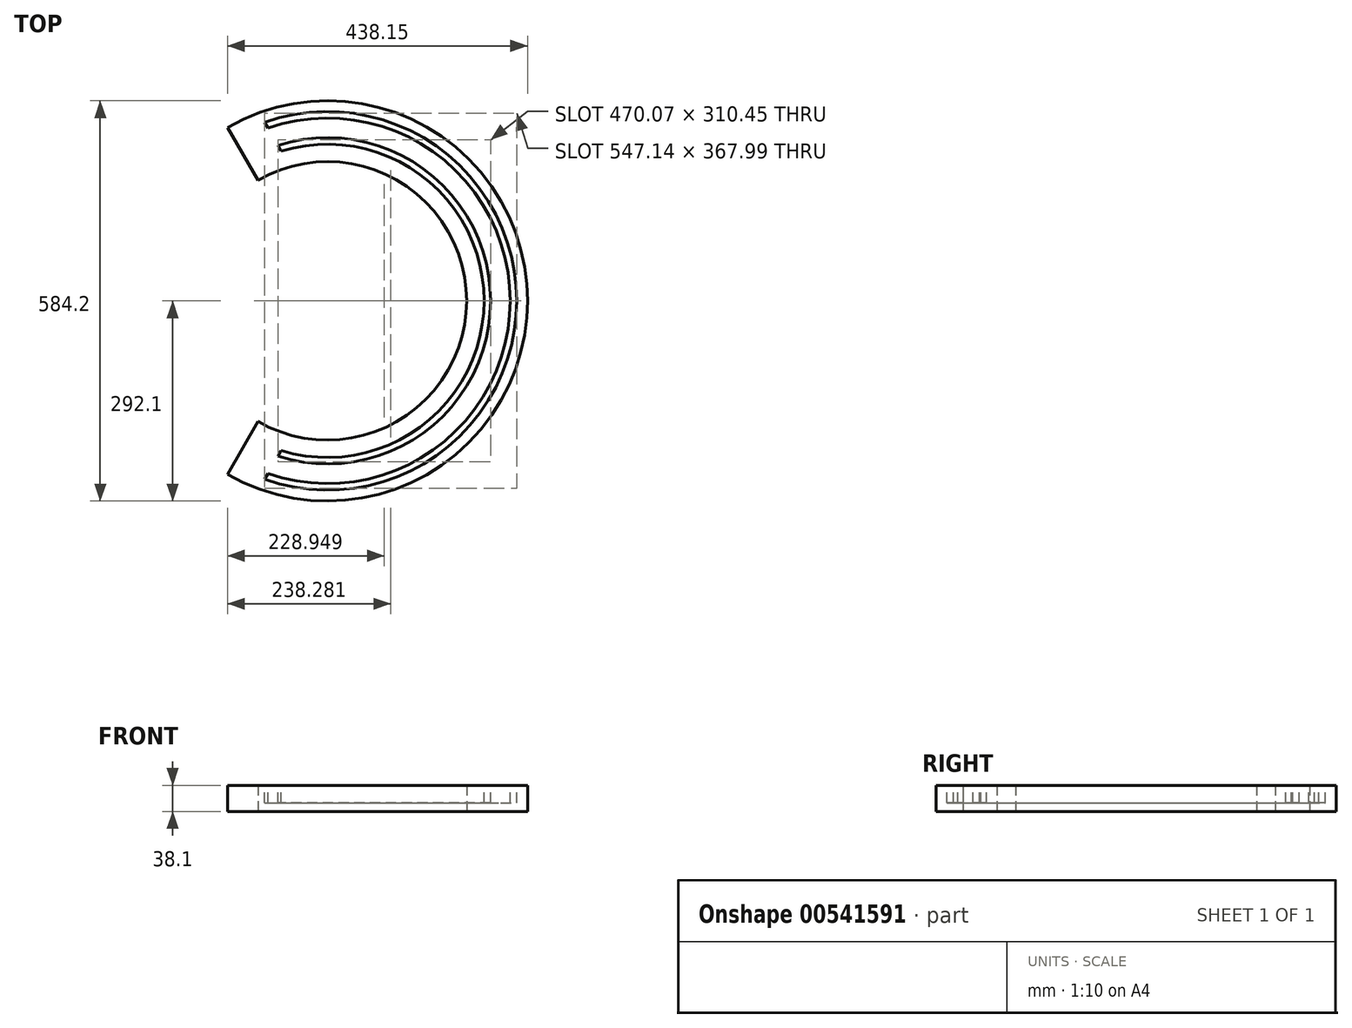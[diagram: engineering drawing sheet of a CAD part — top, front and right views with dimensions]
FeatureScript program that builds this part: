
annotation { "Feature Type Name" : "Feature", "Feature Type Description" : "" }
export const myFeature = defineFeature(function(context is Context, id is Id, definition is map)
    precondition{}
    {
        {
            var Q0;
            Q0=qCreatedBy(makeId("Top.planeOp"),FACE);
            var sketch = newSketch(context, id + "F0", { "sketchPlane" : qUnion([Q0])});
            skArc(sketch, "E0", {"start": v(-101.6, -175.98) * mm, "mid": v(203.2, 0) * mm, "end": v(-101.6, 175.98) * mm});
            skArc(sketch, "E1", {"start": v(-146.05, -252.97) * mm, "mid": v(292.1, 0) * mm, "end": v(-146.05, 252.97) * mm});
            skLineSegment(sketch, "E2", {"start": v(-101.6, -175.98) * mm, "end": v(-146.05, -252.97) * mm});
            skLineSegment(sketch, "E3", {"start": v(-101.6, 175.98) * mm, "end": v(-146.05, 252.97) * mm});
            skSolve(sketch);
        }
        {
            var Q0;
            Q0=makeQuery(id+"F0.imprint","IMPRINT",FACE,{"disambiguationData":[TD([[makeQuery(id+"F0.imprint","IMPRINT",EDGE,{"derivedFrom":sQuery(id+"F0.wireOp",EDGE,"E0")}),-1.0]])]});
            extrude(context, id + "F1", {"entities" : qUnion([Q0]), "depth" : 38.1 * mm, "offsetDistance" : 25.4 * mm});
        }
        {
            var Q0;
            Q0=makeQuery(id+"F1.opExtrude","CAP_FACE",FACE,{"disambiguationData":[OSD([sQuery(id+"F0.wireOp",EDGE,"E0"),sQuery(id+"F0.wireOp",EDGE,"E1"),sQuery(id+"F0.wireOp",EDGE,"E2"),sQuery(id+"F0.wireOp",EDGE,"E3")])],"isStart":false});
            var sketch = newSketch(context, id + "F2", { "sketchPlane" : qUnion([Q0])});
            skArc(sketch, "E4", {"start": v(-67.45, -218.42) * mm, "mid": v(228.6, 0) * mm, "end": v(-67.45, 218.42) * mm});
            skLineSegment(sketch, "E5", {"start": v(-101.6, 175.98) * mm, "end": v(-146.05, 252.97) * mm});
            skLineSegment(sketch, "E6", {"start": v(-101.6, -175.98) * mm, "end": v(-146.05, -252.97) * mm});
            skArc(sketch, "E7", {"start": v(-72.33, -226.87) * mm, "mid": v(238.13, 0) * mm, "end": v(-72.33, 226.87) * mm});
            skArc(sketch, "E8", {"start": v(-86.91, -252.14) * mm, "mid": v(266.7, 0) * mm, "end": v(-86.91, 252.14) * mm});
            skArc(sketch, "E9", {"start": v(-91.76, -260.54) * mm, "mid": v(276.23, 0) * mm, "end": v(-91.76, 260.54) * mm});
            skLineSegment(sketch, "E10", {"start": v(-91.76, -260.54) * mm, "end": v(-86.91, -252.14) * mm});
            skLineSegment(sketch, "E11", {"start": v(-91.76, 260.54) * mm, "end": v(-86.91, 252.14) * mm});
            skPoint(sketch, "E12.orphan", {"position": v(0, -337.29) * mm});
            skLineSegment(sketch, "E13.trimOffspring", {"start": v(-72.33, -226.87) * mm, "end": v(-67.45, -218.42) * mm});
            skPoint(sketch, "E14.orphan", {"position": v(0, 337.29) * mm});
            skLineSegment(sketch, "E15.trimOffspring", {"start": v(-72.33, 226.87) * mm, "end": v(-67.45, 218.42) * mm});
            skSolve(sketch);
        }
        {
            var Q0;
            Q0=makeQuery(id+"F2.imprint","IMPRINT",FACE,{"disambiguationData":[TD([[makeQuery(id+"F2.imprint","IMPRINT",EDGE,{"derivedFrom":sQuery(id+"F2.wireOp",EDGE,"E4")}),-1.0]])]});
            var Q1;
            Q1=makeQuery(id+"F2.imprint","IMPRINT",FACE,{"disambiguationData":[TD([[makeQuery(id+"F2.imprint","IMPRINT",EDGE,{"derivedFrom":sQuery(id+"F2.wireOp",EDGE,"E8")}),-1.0]])]});
            extrude(context, id + "F3", {"entities" : qUnion([Q0, Q1]), "operationType" : NewBodyOperationType.REMOVE, "oppositeDirection" : true, "depth" : 25.4 * mm, "offsetDistance" : 25.4 * mm});
        }
    });
